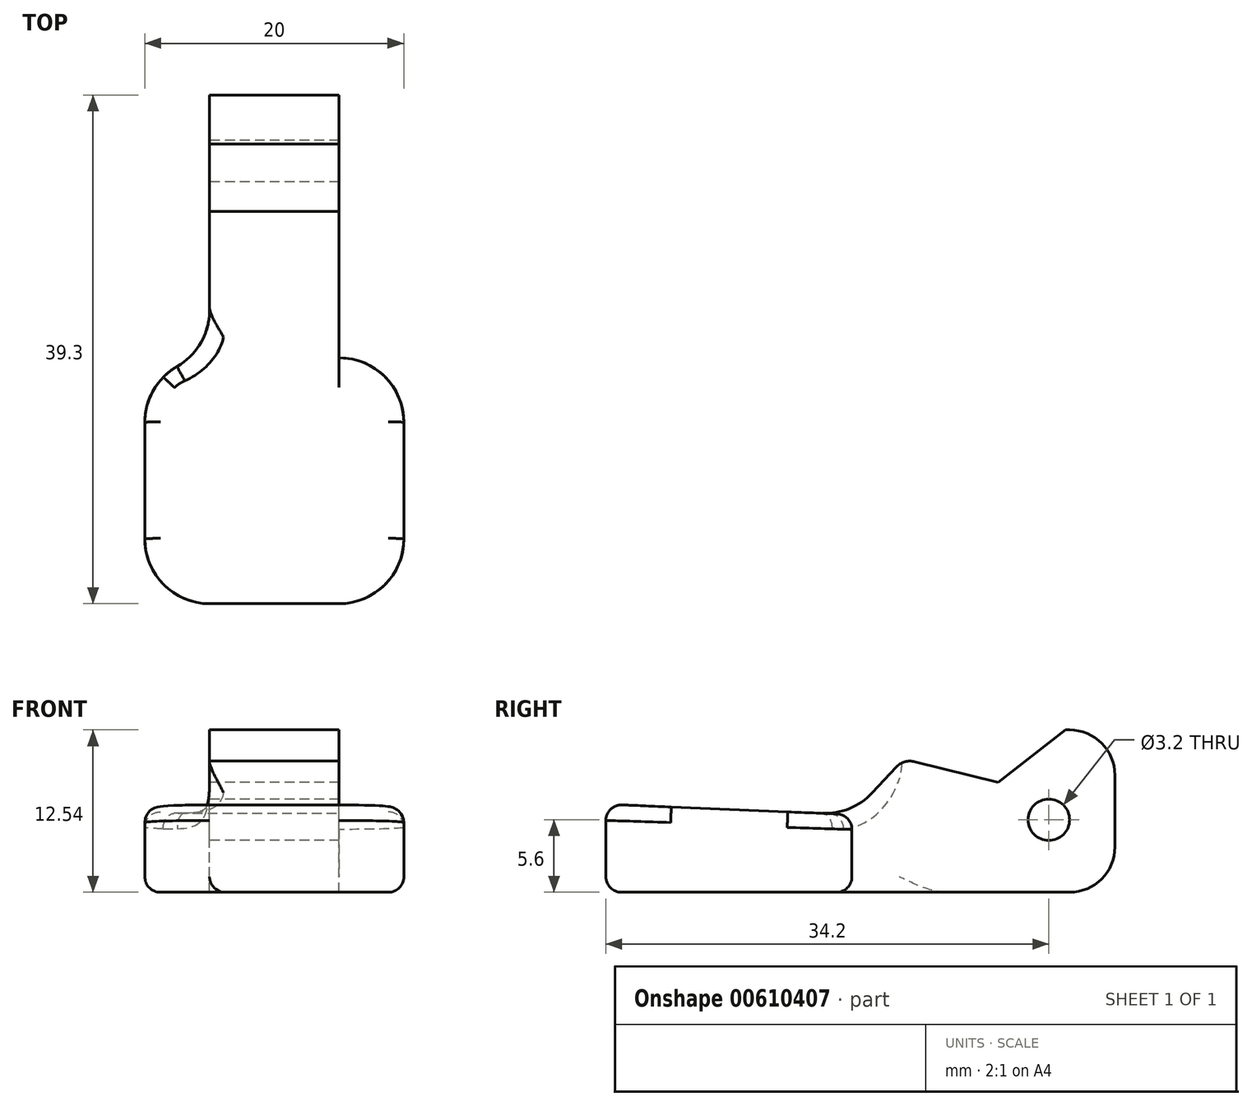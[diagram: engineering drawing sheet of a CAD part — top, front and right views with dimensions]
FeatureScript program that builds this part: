
annotation { "Feature Type Name" : "Feature", "Feature Type Description" : "" }
export const myFeature = defineFeature(function(context is Context, id is Id, definition is map)
    precondition{}
    {
        {
            var Q0;
            Q0=qCreatedBy(makeId("Right.planeOp"),FACE);
            var sketch = newSketch(context, id + "F0", { "sketchPlane" : qUnion([Q0])});
            skLineSegment(sketch, "E0", {"start": v(0, 0) * mm, "end": v(39.3, 0) * mm});
            skLineSegment(sketch, "E1", {"start": v(39.3, 0) * mm, "end": v(39.3, 12.54) * mm});
            skLineSegment(sketch, "E2", {"start": v(39.3, 12.54) * mm, "end": v(35.5, 12.54) * mm});
            skLineSegment(sketch, "E3", {"start": v(35.5, 12.54) * mm, "end": v(30.3, 8.5) * mm});
            skLineSegment(sketch, "E4", {"start": v(30.3, 8.5) * mm, "end": v(23, 10.3) * mm});
            skLineSegment(sketch, "E5", {"start": v(23, 10.3) * mm, "end": v(19, 6) * mm});
            skLineSegment(sketch, "E6", {"start": v(19, 6) * mm, "end": v(0, 6.8) * mm});
            skLineSegment(sketch, "E7", {"start": v(0, 6.8) * mm, "end": v(0, 0) * mm});
            skLineSegment(sketch, "E8", {"start": v(19, 6) * mm, "end": v(19, 0) * mm});
            skCircle(sketch, "E9", {"center": v(34.2, 5.6) * mm, "radius": 1.6 * mm});
            skSolve(sketch);
        }
        {
            assignVariable(context, id + "F1", {"name" : "TabWidth", "anyValue" : 10});
        }
        {
            assignVariable(context, id + "F2", {"name" : "ClipWidth", "anyValue" : 5});
        }
        {
            var Q0;
            Q0=makeQuery(id+"F0.imprint","IMPRINT",FACE,{"disambiguationData":[TD([[makeQuery(id+"F0.imprint","IMPRINT",EDGE,{"derivedFrom":sQuery(id+"F0.wireOp",EDGE,"E6")}),1.0]])]});
            extrude(context, id + "F3", {"entities" : qUnion([Q0]), "depth" : getVariable(context, 'TabWidth') * mm, "offsetDistance" : 25 * mm, "hasSecondDirection" : true, "secondDirectionOppositeDirection" : true, "secondDirectionDepth" : getVariable(context, 'TabWidth') * mm});
        }
        {
            var Q0;
            {var subQ0=sQuery(id+"F0.wireOp",EDGE,"E1");Q0=makeQuery(id+"F0.imprint","IMPRINT",FACE,{"disambiguationData":[TD([[makeQuery(id+"F0.imprint","IMPRINT",EDGE,{"derivedFrom":subQ0}),1.0]])]});}
            extrude(context, id + "F4", {"entities" : qUnion([Q0]), "operationType" : NewBodyOperationType.ADD, "depth" : getVariable(context, 'ClipWidth') * mm, "offsetDistance" : 25 * mm, "hasSecondDirection" : true, "secondDirectionOppositeDirection" : true, "secondDirectionDepth" : getVariable(context, 'ClipWidth') * mm});
        }
        {
            var Q0;
            Q0=makeQuery(id+"F3.opExtrude","CAP_EDGE",EDGE,{"disambiguationData":[OSD([sQuery(id+"F0.wireOp",EDGE,"E7")])],"isStart":false});
            var Q1;
            Q1=makeQuery(id+"F3.opExtrude","CAP_EDGE",EDGE,{"disambiguationData":[OSD([sQuery(id+"F0.wireOp",EDGE,"E8")])],"isStart":false});
            var Q2;
            Q2=makeQuery(id+"F4.opExtrude","CAP_EDGE",EDGE,{"disambiguationData":[OSD([sQuery(id+"F0.wireOp",EDGE,"E8")])],"isStart":false});
            var Q3;
            {var subQ0=sQuery(id+"F0.wireOp",EDGE,"E8");var subQ1=sQuery(id+"F0.wireOp",EDGE,"E6");var subQ2=sQuery(id+"F0.wireOp",EDGE,"E5");Q3=makeQuery(id+"F4.boolean.opBoolean","MERGE",EDGE,{"derivedFrom":[makeQuery(id+"F3.opExtrude","SWEPT_EDGE",EDGE,{"disambiguationData":[OSD([subQ2,subQ1,subQ0])]}),makeQuery(id+"F4.opExtrude","SWEPT_EDGE",EDGE,{"disambiguationData":[OSD([subQ2,subQ1,subQ0])]})]});}
            var Q4;
            Q4=makeQuery(id+"F3.opExtrude","CAP_EDGE",EDGE,{"disambiguationData":[OSD([sQuery(id+"F0.wireOp",EDGE,"E7")])],"isStart":true});
            var Q5;
            Q5=makeQuery(id+"F3.opExtrude","CAP_EDGE",EDGE,{"disambiguationData":[OSD([sQuery(id+"F0.wireOp",EDGE,"E8")])],"isStart":true});
            var Q6;
            Q6=makeQuery(id+"F4.opExtrude","CAP_EDGE",EDGE,{"disambiguationData":[OSD([sQuery(id+"F0.wireOp",EDGE,"E8")])],"isStart":true});
            fillet(context, id + "F5", {"entities" : qUnion([Q0, Q1, Q2, Q3, Q4, Q5, Q6]), "radius" : 5 * mm, "tangentPropagation" : true, "allowEdgeOverflow" : false});
        }
        {
            var Q0;
            Q0=makeQuery(id+"F3.opExtrude","SWEPT_EDGE",EDGE,{"disambiguationData":[OSD([sQuery(id+"F0.wireOp",EDGE,"E6"),sQuery(id+"F0.wireOp",EDGE,"E7")])]});
            var Q1;
            Q1=makeQuery(id+"F5.opFillet","BLEND_EDGE",EDGE,{"blendedFrom":[makeQuery(id+"F3.opExtrude","CAP_EDGE",EDGE,{"disambiguationData":[OSD([sQuery(id+"F0.wireOp",EDGE,"E7")])],"isStart":false}),makeQuery(id+"F3.opExtrude","SWEPT_FACE",FACE,{"disambiguationData":[OSD([sQuery(id+"F0.wireOp",EDGE,"E6")])]})],"blendedInto":[makeQuery(id+"F3.opExtrude","SWEPT_FACE",FACE,{"disambiguationData":[OSD([sQuery(id+"F0.wireOp",EDGE,"E6")])]})]});
            var Q2;
            Q2=makeQuery(id+"F3.opExtrude","CAP_EDGE",EDGE,{"disambiguationData":[OSD([sQuery(id+"F0.wireOp",EDGE,"E6")])],"isStart":false});
            var Q3;
            Q3=makeQuery(id+"F3.opExtrude","CAP_EDGE",EDGE,{"disambiguationData":[OSD([sQuery(id+"F0.wireOp",EDGE,"E6")])],"isStart":true});
            var Q4;
            Q4=makeQuery(id+"F5.opFillet","BLEND_EDGE",EDGE,{"blendedFrom":[makeQuery(id+"F3.opExtrude","CAP_EDGE",EDGE,{"disambiguationData":[OSD([sQuery(id+"F0.wireOp",EDGE,"E7")])],"isStart":true}),makeQuery(id+"F3.opExtrude","SWEPT_FACE",FACE,{"disambiguationData":[OSD([sQuery(id+"F0.wireOp",EDGE,"E6")])]})],"blendedInto":[makeQuery(id+"F3.opExtrude","SWEPT_FACE",FACE,{"disambiguationData":[OSD([sQuery(id+"F0.wireOp",EDGE,"E6")])]})]});
            var Q5;
            Q5=makeQuery(id+"F3.opExtrude","SWEPT_EDGE",EDGE,{"disambiguationData":[OSD([sQuery(id+"F0.wireOp",EDGE,"E0"),sQuery(id+"F0.wireOp",EDGE,"E7")])]});
            var Q6;
            {var subQ0=sQuery(id+"F0.wireOp",EDGE,"E0");Q6=makeQuery(id+"F5.opFillet","BLEND_EDGE",EDGE,{"blendedFrom":[makeQuery(id+"F3.opExtrude","CAP_EDGE",EDGE,{"disambiguationData":[OSD([sQuery(id+"F0.wireOp",EDGE,"E7")])],"isStart":false}),makeQuery(id+"F4.boolean.opBoolean","MERGE",FACE,{"derivedFrom":[makeQuery(id+"F3.opExtrude","SWEPT_FACE",FACE,{"disambiguationData":[OSD([subQ0])]}),makeQuery(id+"F4.opExtrude","SWEPT_FACE",FACE,{"disambiguationData":[OSD([subQ0])]})]})],"blendedInto":[makeQuery(id+"F4.boolean.opBoolean","MERGE",FACE,{"derivedFrom":[makeQuery(id+"F3.opExtrude","SWEPT_FACE",FACE,{"disambiguationData":[OSD([subQ0])]}),makeQuery(id+"F4.opExtrude","SWEPT_FACE",FACE,{"disambiguationData":[OSD([subQ0])]})]})]});}
            var Q7;
            Q7=makeQuery(id+"F3.opExtrude","CAP_EDGE",EDGE,{"disambiguationData":[OSD([sQuery(id+"F0.wireOp",EDGE,"E0")])],"isStart":false});
            var Q8;
            {var subQ0=sQuery(id+"F0.wireOp",EDGE,"E0");Q8=makeQuery(id+"F5.opFillet","BLEND_EDGE",EDGE,{"blendedFrom":[makeQuery(id+"F3.opExtrude","CAP_EDGE",EDGE,{"disambiguationData":[OSD([sQuery(id+"F0.wireOp",EDGE,"E7")])],"isStart":true}),makeQuery(id+"F4.boolean.opBoolean","MERGE",FACE,{"derivedFrom":[makeQuery(id+"F3.opExtrude","SWEPT_FACE",FACE,{"disambiguationData":[OSD([subQ0])]}),makeQuery(id+"F4.opExtrude","SWEPT_FACE",FACE,{"disambiguationData":[OSD([subQ0])]})]})],"blendedInto":[makeQuery(id+"F4.boolean.opBoolean","MERGE",FACE,{"derivedFrom":[makeQuery(id+"F3.opExtrude","SWEPT_FACE",FACE,{"disambiguationData":[OSD([subQ0])]}),makeQuery(id+"F4.opExtrude","SWEPT_FACE",FACE,{"disambiguationData":[OSD([subQ0])]})]})]});}
            var Q9;
            Q9=makeQuery(id+"F3.opExtrude","CAP_EDGE",EDGE,{"disambiguationData":[OSD([sQuery(id+"F0.wireOp",EDGE,"E0")])],"isStart":true});
            var Q10;
            {var subQ0=sQuery(id+"F0.wireOp",EDGE,"E8");var subQ1=sQuery(id+"F0.wireOp",EDGE,"E6");var subQ2=sQuery(id+"F0.wireOp",EDGE,"E5");Q10=makeQuery(id+"F5.opFillet","BLEND_EDGE",EDGE,{"disambiguationData":[OD(1.0)],"blendedFrom":[makeQuery(id+"F4.boolean.opBoolean","MERGE",EDGE,{"derivedFrom":[makeQuery(id+"F3.opExtrude","SWEPT_EDGE",EDGE,{"disambiguationData":[OSD([subQ2,subQ1,subQ0])]}),makeQuery(id+"F4.opExtrude","SWEPT_EDGE",EDGE,{"disambiguationData":[OSD([subQ2,subQ1,subQ0])]})]})],"blendedInto":[]});}
            var Q11;
            {var subQ0=sQuery(id+"F0.wireOp",EDGE,"E8");var subQ1=sQuery(id+"F0.wireOp",EDGE,"E6");var subQ2=sQuery(id+"F0.wireOp",EDGE,"E5");Q11=makeQuery(id+"F5.opFillet","BLEND_EDGE",EDGE,{"disambiguationData":[OD(0.0)],"blendedFrom":[makeQuery(id+"F3.opExtrude","CAP_EDGE",EDGE,{"disambiguationData":[OSD([subQ0])],"isStart":false}),makeQuery(id+"F4.boolean.opBoolean","MERGE",EDGE,{"derivedFrom":[makeQuery(id+"F3.opExtrude","SWEPT_EDGE",EDGE,{"disambiguationData":[OSD([subQ2,subQ1,subQ0])]}),makeQuery(id+"F4.opExtrude","SWEPT_EDGE",EDGE,{"disambiguationData":[OSD([subQ2,subQ1,subQ0])]})]})],"blendedInto":[]});}
            var Q12;
            {var subQ0=sQuery(id+"F0.wireOp",EDGE,"E0");Q12=makeQuery(id+"F5.opFillet","BLEND_EDGE",EDGE,{"blendedFrom":[makeQuery(id+"F3.opExtrude","CAP_EDGE",EDGE,{"disambiguationData":[OSD([sQuery(id+"F0.wireOp",EDGE,"E8")])],"isStart":false}),makeQuery(id+"F4.boolean.opBoolean","MERGE",FACE,{"derivedFrom":[makeQuery(id+"F3.opExtrude","SWEPT_FACE",FACE,{"disambiguationData":[OSD([subQ0])]}),makeQuery(id+"F4.opExtrude","SWEPT_FACE",FACE,{"disambiguationData":[OSD([subQ0])]})]})],"blendedInto":[makeQuery(id+"F4.boolean.opBoolean","MERGE",FACE,{"derivedFrom":[makeQuery(id+"F3.opExtrude","SWEPT_FACE",FACE,{"disambiguationData":[OSD([subQ0])]}),makeQuery(id+"F4.opExtrude","SWEPT_FACE",FACE,{"disambiguationData":[OSD([subQ0])]})]})]});}
            var Q13;
            {var subQ0=sQuery(id+"F0.wireOp",EDGE,"E0");var subQ1=sQuery(id+"F0.wireOp",EDGE,"E8");var subQ2=sQuery(id+"F0.wireOp",EDGE,"E6");var subQ3=sQuery(id+"F0.wireOp",EDGE,"E5");Q13=makeQuery(id+"F5.opFillet","BLEND_EDGE",EDGE,{"disambiguationData":[OD(1.0)],"blendedFrom":[makeQuery(id+"F4.boolean.opBoolean","MERGE",EDGE,{"derivedFrom":[makeQuery(id+"F3.opExtrude","SWEPT_EDGE",EDGE,{"disambiguationData":[OSD([subQ3,subQ2,subQ1])]}),makeQuery(id+"F4.opExtrude","SWEPT_EDGE",EDGE,{"disambiguationData":[OSD([subQ3,subQ2,subQ1])]})]}),makeQuery(id+"F4.boolean.opBoolean","MERGE",FACE,{"derivedFrom":[makeQuery(id+"F3.opExtrude","SWEPT_FACE",FACE,{"disambiguationData":[OSD([subQ0])]}),makeQuery(id+"F4.opExtrude","SWEPT_FACE",FACE,{"disambiguationData":[OSD([subQ0])]})]})],"blendedInto":[makeQuery(id+"F4.boolean.opBoolean","MERGE",FACE,{"derivedFrom":[makeQuery(id+"F3.opExtrude","SWEPT_FACE",FACE,{"disambiguationData":[OSD([subQ0])]}),makeQuery(id+"F4.opExtrude","SWEPT_FACE",FACE,{"disambiguationData":[OSD([subQ0])]})]})]});}
            var Q14;
            Q14=makeQuery(id+"F5.opFillet","BLEND_EDGE",EDGE,{"blendedFrom":[makeQuery(id+"F3.opExtrude","CAP_EDGE",EDGE,{"disambiguationData":[OSD([sQuery(id+"F0.wireOp",EDGE,"E8")])],"isStart":false}),makeQuery(id+"F3.opExtrude","SWEPT_FACE",FACE,{"disambiguationData":[OSD([sQuery(id+"F0.wireOp",EDGE,"E6")])]})],"blendedInto":[makeQuery(id+"F3.opExtrude","SWEPT_FACE",FACE,{"disambiguationData":[OSD([sQuery(id+"F0.wireOp",EDGE,"E6")])]})]});
            var Q15;
            Q15=makeQuery(id+"F5.opFillet","BLEND_EDGE",EDGE,{"blendedFrom":[makeQuery(id+"F3.opExtrude","CAP_EDGE",EDGE,{"disambiguationData":[OSD([sQuery(id+"F0.wireOp",EDGE,"E8")])],"isStart":true}),makeQuery(id+"F3.opExtrude","SWEPT_FACE",FACE,{"disambiguationData":[OSD([sQuery(id+"F0.wireOp",EDGE,"E6")])]})],"blendedInto":[makeQuery(id+"F3.opExtrude","SWEPT_FACE",FACE,{"disambiguationData":[OSD([sQuery(id+"F0.wireOp",EDGE,"E6")])]})]});
            var Q16;
            {var subQ0=sQuery(id+"F0.wireOp",EDGE,"E8");var subQ1=sQuery(id+"F0.wireOp",EDGE,"E6");var subQ2=sQuery(id+"F0.wireOp",EDGE,"E5");Q16=makeQuery(id+"F5.opFillet","BLEND_EDGE",EDGE,{"disambiguationData":[OD(0.0)],"blendedFrom":[makeQuery(id+"F3.opExtrude","CAP_EDGE",EDGE,{"disambiguationData":[OSD([subQ0])],"isStart":true}),makeQuery(id+"F4.boolean.opBoolean","MERGE",EDGE,{"derivedFrom":[makeQuery(id+"F3.opExtrude","SWEPT_EDGE",EDGE,{"disambiguationData":[OSD([subQ2,subQ1,subQ0])]}),makeQuery(id+"F4.opExtrude","SWEPT_EDGE",EDGE,{"disambiguationData":[OSD([subQ2,subQ1,subQ0])]})]})],"blendedInto":[]});}
            var Q17;
            {var subQ0=sQuery(id+"F0.wireOp",EDGE,"E8");var subQ1=sQuery(id+"F0.wireOp",EDGE,"E6");var subQ2=sQuery(id+"F0.wireOp",EDGE,"E5");Q17=makeQuery(id+"F5.opFillet","BLEND_EDGE",EDGE,{"disambiguationData":[OD(0.0)],"blendedFrom":[makeQuery(id+"F4.boolean.opBoolean","MERGE",EDGE,{"derivedFrom":[makeQuery(id+"F3.opExtrude","SWEPT_EDGE",EDGE,{"disambiguationData":[OSD([subQ2,subQ1,subQ0])]}),makeQuery(id+"F4.opExtrude","SWEPT_EDGE",EDGE,{"disambiguationData":[OSD([subQ2,subQ1,subQ0])]})]})],"blendedInto":[]});}
            var Q18;
            {var subQ0=sQuery(id+"F0.wireOp",EDGE,"E0");Q18=makeQuery(id+"F5.opFillet","BLEND_EDGE",EDGE,{"blendedFrom":[makeQuery(id+"F3.opExtrude","CAP_EDGE",EDGE,{"disambiguationData":[OSD([sQuery(id+"F0.wireOp",EDGE,"E8")])],"isStart":true}),makeQuery(id+"F4.boolean.opBoolean","MERGE",FACE,{"derivedFrom":[makeQuery(id+"F3.opExtrude","SWEPT_FACE",FACE,{"disambiguationData":[OSD([subQ0])]}),makeQuery(id+"F4.opExtrude","SWEPT_FACE",FACE,{"disambiguationData":[OSD([subQ0])]})]})],"blendedInto":[makeQuery(id+"F4.boolean.opBoolean","MERGE",FACE,{"derivedFrom":[makeQuery(id+"F3.opExtrude","SWEPT_FACE",FACE,{"disambiguationData":[OSD([subQ0])]}),makeQuery(id+"F4.opExtrude","SWEPT_FACE",FACE,{"disambiguationData":[OSD([subQ0])]})]})]});}
            var Q19;
            {var subQ0=sQuery(id+"F0.wireOp",EDGE,"E0");var subQ1=sQuery(id+"F0.wireOp",EDGE,"E8");var subQ2=sQuery(id+"F0.wireOp",EDGE,"E6");var subQ3=sQuery(id+"F0.wireOp",EDGE,"E5");Q19=makeQuery(id+"F5.opFillet","BLEND_EDGE",EDGE,{"disambiguationData":[OD(0.0)],"blendedFrom":[makeQuery(id+"F4.boolean.opBoolean","MERGE",EDGE,{"derivedFrom":[makeQuery(id+"F3.opExtrude","SWEPT_EDGE",EDGE,{"disambiguationData":[OSD([subQ3,subQ2,subQ1])]}),makeQuery(id+"F4.opExtrude","SWEPT_EDGE",EDGE,{"disambiguationData":[OSD([subQ3,subQ2,subQ1])]})]}),makeQuery(id+"F4.boolean.opBoolean","MERGE",FACE,{"derivedFrom":[makeQuery(id+"F3.opExtrude","SWEPT_FACE",FACE,{"disambiguationData":[OSD([subQ0])]}),makeQuery(id+"F4.opExtrude","SWEPT_FACE",FACE,{"disambiguationData":[OSD([subQ0])]})]})],"blendedInto":[makeQuery(id+"F4.boolean.opBoolean","MERGE",FACE,{"derivedFrom":[makeQuery(id+"F3.opExtrude","SWEPT_FACE",FACE,{"disambiguationData":[OSD([subQ0])]}),makeQuery(id+"F4.opExtrude","SWEPT_FACE",FACE,{"disambiguationData":[OSD([subQ0])]})]})]});}
            fillet(context, id + "F6", {"entities" : qUnion([Q0, Q1, Q2, Q3, Q4, Q5, Q6, Q7, Q8, Q9, Q10, Q11, Q12, Q13, Q14, Q15, Q16, Q17, Q18, Q19]), "radius" : 1.2 * mm, "allowEdgeOverflow" : false});
        }
        {
            var Q0;
            Q0=makeQuery(id+"F4.opExtrude","SWEPT_EDGE",EDGE,{"disambiguationData":[OSD([sQuery(id+"F0.wireOp",EDGE,"E1"),sQuery(id+"F0.wireOp",EDGE,"E2")])]});
            var Q1;
            Q1=makeQuery(id+"F4.opExtrude","SWEPT_EDGE",EDGE,{"disambiguationData":[OSD([sQuery(id+"F0.wireOp",EDGE,"E0"),sQuery(id+"F0.wireOp",EDGE,"E1")])]});
            fillet(context, id + "F7", {"entities" : qUnion([Q0, Q1]), "radius" : 3.5 * mm, "tangentPropagation" : true, "allowEdgeOverflow" : false});
        }
        {
            var Q0;
            Q0=makeQuery(id+"F4.opExtrude","SWEPT_EDGE",EDGE,{"disambiguationData":[OSD([sQuery(id+"F0.wireOp",EDGE,"E4"),sQuery(id+"F0.wireOp",EDGE,"E5")])]});
            fillet(context, id + "F8", {"entities" : qUnion([Q0]), "radius" : 1.5 * mm, "tangentPropagation" : true, "allowEdgeOverflow" : false});
        }
    });
